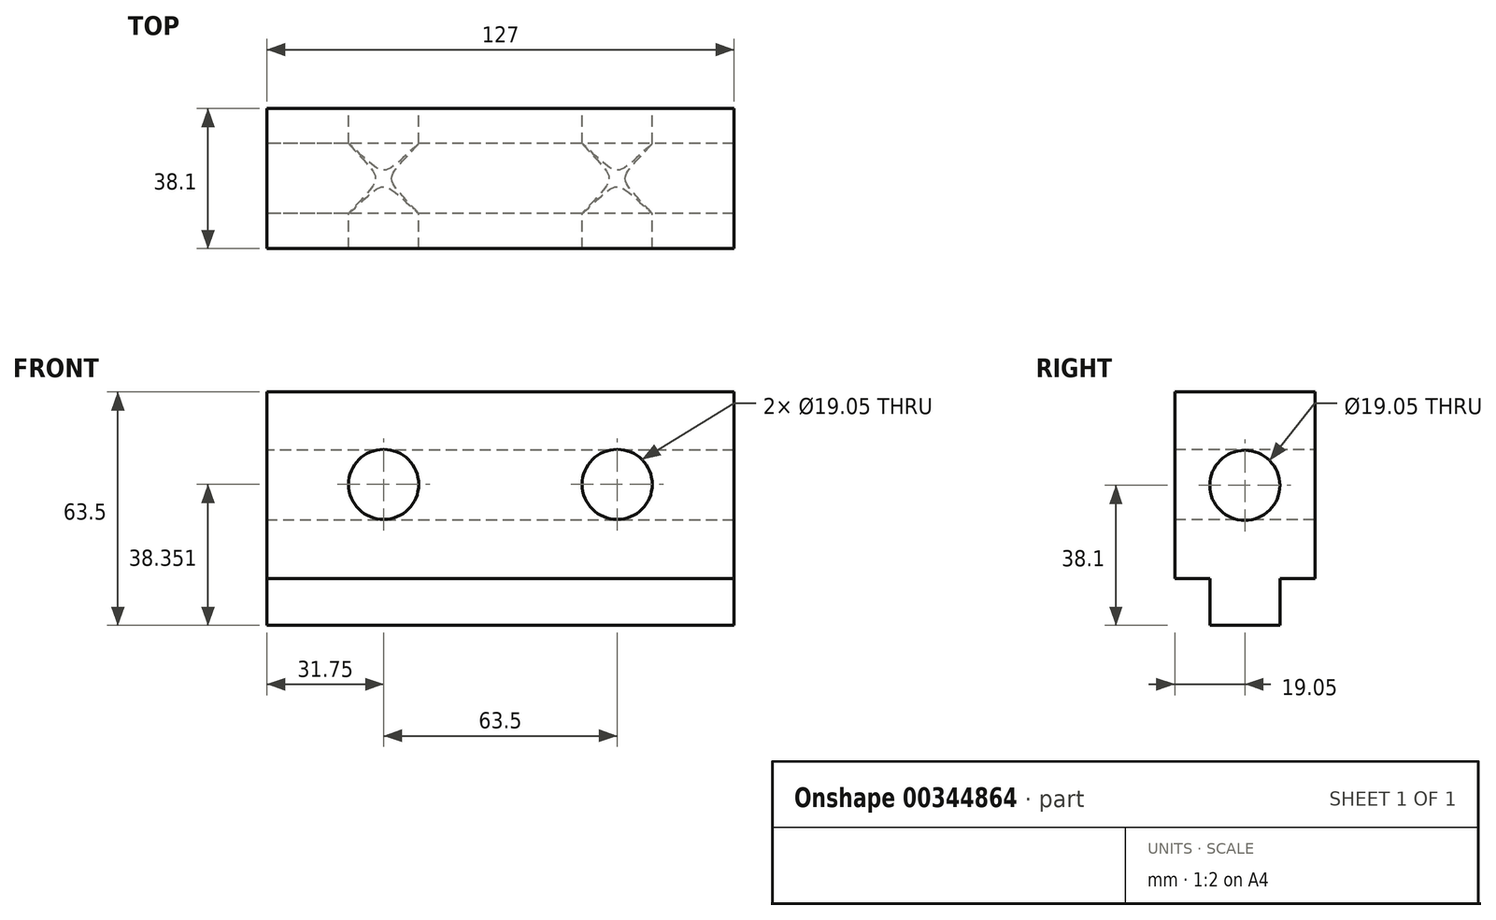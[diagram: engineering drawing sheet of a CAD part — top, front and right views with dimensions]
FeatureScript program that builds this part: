
annotation { "Feature Type Name" : "Feature", "Feature Type Description" : "" }
export const myFeature = defineFeature(function(context is Context, id is Id, definition is map)
    precondition{}
    {
        {
            var Q0;
            Q0=qCreatedBy(makeId("Right.planeOp"),FACE);
            var sketch = newSketch(context, id + "F0", { "sketchPlane" : qUnion([Q0])});
            skLineSegment(sketch, "E0.bottom", {"start": v(19.05, 31.75) * mm, "end": v(-19.05, 31.75) * mm});
            skLineSegment(sketch, "E0.top", {"start": v(9.53, -31.75) * mm, "end": v(-9.53, -31.75) * mm});
            skLineSegment(sketch, "E0.left", {"start": v(19.05, 31.75) * mm, "end": v(19.05, -19.05) * mm});
            skLineSegment(sketch, "E0.right", {"start": v(-19.05, 31.75) * mm, "end": v(-19.05, -19.05) * mm});
            skPoint(sketch, "E0.middle", {"position": v(0, 0) * mm});
            skLineSegment(sketch, "E1", {"start": v(-19.05, -19.05) * mm, "end": v(-9.53, -19.05) * mm});
            skLineSegment(sketch, "E2", {"start": v(-9.53, -19.05) * mm, "end": v(-9.53, -31.75) * mm});
            skLineSegment(sketch, "E3", {"start": v(19.05, -19.05) * mm, "end": v(9.52, -19.05) * mm});
            skLineSegment(sketch, "E4", {"start": v(9.52, -19.05) * mm, "end": v(9.53, -31.75) * mm});
            skPoint(sketch, "E5.orphan", {"position": v(-19.05, -31.75) * mm});
            skPoint(sketch, "E6.orphan", {"position": v(19.05, -31.75) * mm});
            skCircle(sketch, "E7", {"center": v(0, 6.35) * mm, "radius": 9.53 * mm});
            skPoint(sketch, "E8.orphan", {"position": v(-19.05, 6.35) * mm});
            skPoint(sketch, "E9.end.orphan", {"position": v(19.05, 6.35) * mm});
            skSolve(sketch);
        }
        {
            var Q0;
            Q0 = qSketchRegion(id + "F0", true);
            extrude(context, id + "F1", {"entities" : qUnion([Q0]), "depth" : 127 * mm});
        }
        {
            var Q0;
            Q0=qCreatedBy(makeId("Front.planeOp"),FACE);
            var sketch = newSketch(context, id + "F2", { "sketchPlane" : qUnion([Q0])});
            skCircle(sketch, "E10", {"center": v(31.75, 6.6) * mm, "radius": 9.53 * mm});
            skCircle(sketch, "E11.MirrorC", {"center": v(95.25, 6.6) * mm, "radius": 9.53 * mm});
            skPoint(sketch, "E12.start.orphan", {"position": v(0, 6.6) * mm});
            skSolve(sketch);
        }
        {
            var Q0;
            Q0 = qSketchRegion(id + "F2", true);
            extrude(context, id + "F3", {"entities" : qUnion([Q0]), "operationType" : NewBodyOperationType.REMOVE, "depth" : 46.23 * mm, "hasSecondDirection" : true, "secondDirectionOppositeDirection" : true, "secondDirectionDepth" : 48.5 * mm});
        }
    });
